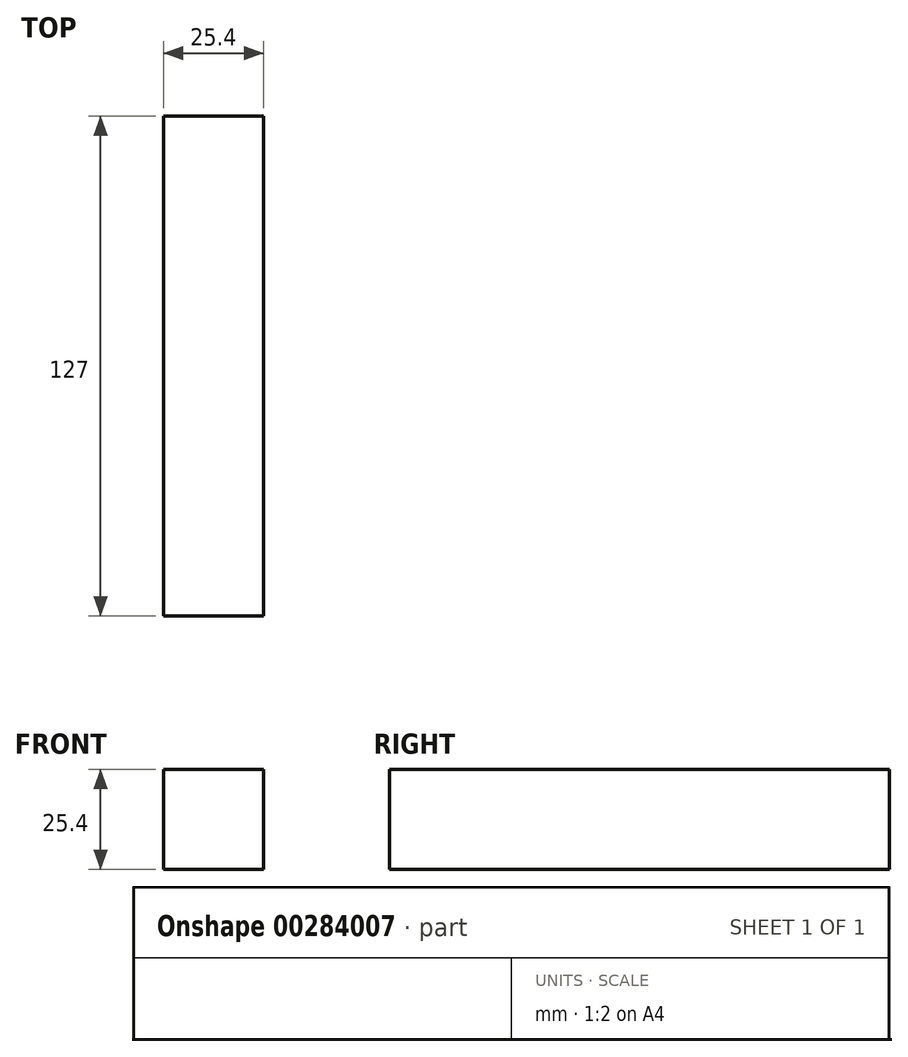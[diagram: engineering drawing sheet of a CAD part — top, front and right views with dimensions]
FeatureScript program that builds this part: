
annotation { "Feature Type Name" : "Feature", "Feature Type Description" : "" }
export const myFeature = defineFeature(function(context is Context, id is Id, definition is map)
    precondition{}
    {
        {
            var Q0;
            Q0=qCreatedBy(makeId("Front.planeOp"),FACE);
            var sketch = newSketch(context, id + "F0", { "sketchPlane" : qUnion([Q0])});
            skLineSegment(sketch, "E0.bottom", {"start": v(-87.84, 61.87) * mm, "end": v(-62.44, 61.87) * mm});
            skLineSegment(sketch, "E0.top", {"start": v(-87.84, 36.47) * mm, "end": v(-62.44, 36.47) * mm});
            skLineSegment(sketch, "E0.left", {"start": v(-87.84, 61.87) * mm, "end": v(-87.84, 36.47) * mm});
            skLineSegment(sketch, "E0.right", {"start": v(-62.44, 61.87) * mm, "end": v(-62.44, 36.47) * mm});
            skSolve(sketch);
        }
        {
            var Q0;
            Q0 = qSketchRegion(id + "F0", true);
            extrude(context, id + "F1", {"entities" : qUnion([Q0]), "depth" : 127 * mm});
        }
    });
